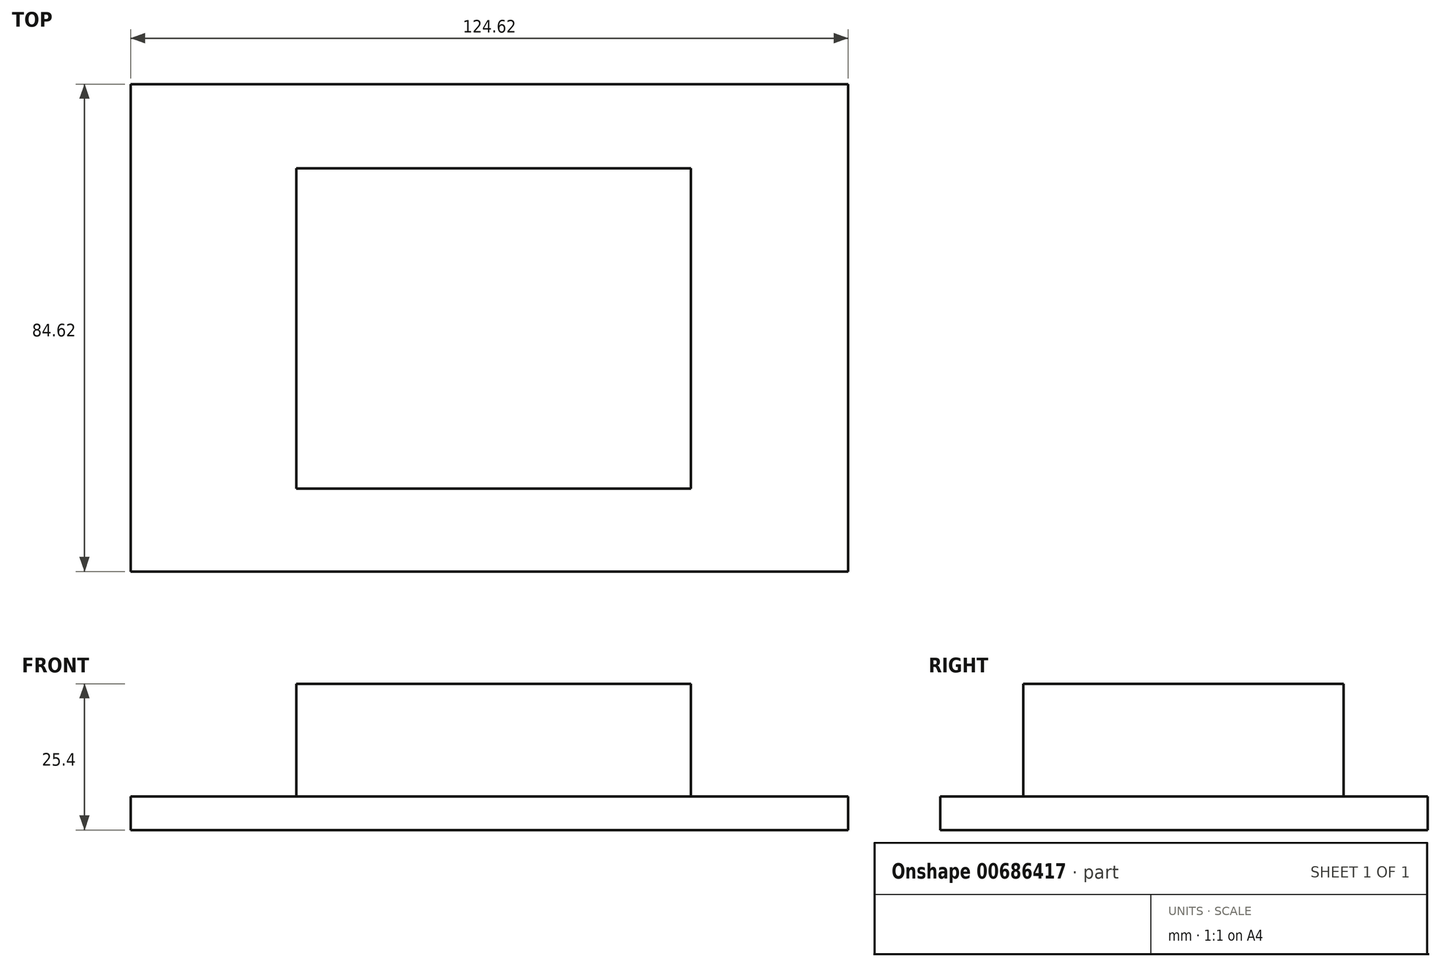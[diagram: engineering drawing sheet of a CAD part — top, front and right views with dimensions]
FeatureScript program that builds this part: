
annotation { "Feature Type Name" : "Feature", "Feature Type Description" : "" }
export const myFeature = defineFeature(function(context is Context, id is Id, definition is map)
    precondition{}
    {
        {
            var Q0;
            Q0=qCreatedBy(makeId("Top.planeOp"),FACE);
            var sketch = newSketch(context, id + "F0", { "sketchPlane" : qUnion([Q0])});
            skLineSegment(sketch, "E0", {"start": v(-37.41, 23.74) * mm, "end": v(-37.41, -32.38) * mm});
            skLineSegment(sketch, "E1", {"start": v(-37.41, -32.38) * mm, "end": v(31.08, -32.38) * mm});
            skLineSegment(sketch, "E2", {"start": v(31.08, -32.1) * mm, "end": v(31.08, 24.03) * mm});
            skLineSegment(sketch, "E3", {"start": v(-37.41, 23.74) * mm, "end": v(31.08, 24.03) * mm});
            skSolve(sketch);
        }
        {
            var Q0;
            Q0=sQuery(id+"F0.wireOp",EDGE,"E2");
            var Q1;
            Q1=sQuery(id+"F0.wireOp",EDGE,"E1");
            var Q2;
            Q2=sQuery(id+"F0.wireOp",EDGE,"E3");
            var Q3;
            Q3=sQuery(id+"F0.wireOp",EDGE,"E0");
            extrude(context, id + "F1", {"bodyType" : ToolBodyType.SURFACE, "surfaceEntities" : qUnion([Q0, Q1, Q2, Q3]), "depth" : 25.4 * mm, "offsetDistance" : 25.4 * mm});
        }
        {
            var Q0;
            Q0=qCreatedBy(makeId("Top.planeOp"),FACE);
            var sketch = newSketch(context, id + "F2", { "sketchPlane" : qUnion([Q0])});
            skLineSegment(sketch, "E4", {"start": v(-66.2, 32.95) * mm, "end": v(-66.2, -46.77) * mm});
            skLineSegment(sketch, "E5", {"start": v(-66.2, -46.77) * mm, "end": v(51.8, -46.77) * mm});
            skLineSegment(sketch, "E6", {"start": v(51.8, -46.77) * mm, "end": v(58.42, -46.77) * mm});
            skLineSegment(sketch, "E7", {"start": v(58.42, -46.77) * mm, "end": v(58.42, 37.85) * mm});
            skLineSegment(sketch, "E8", {"start": v(58.42, 37.85) * mm, "end": v(-66.2, 37.85) * mm});
            skLineSegment(sketch, "E9", {"start": v(-66.2, 32.95) * mm, "end": v(-66.2, 37.85) * mm});
            skSolve(sketch);
        }
        {
            var Q0;
            Q0=makeQuery(id+"F2.imprint","IMPRINT",FACE,{"disambiguationData":[TD([[makeQuery(id+"F2.imprint","IMPRINT",EDGE,{"derivedFrom":sQuery(id+"F2.wireOp",EDGE,"E4")}),1.0]])]});
            extrude(context, id + "F3", {"entities" : qUnion([Q0]), "depth" : 5.84 * mm, "offsetDistance" : 25.4 * mm});
        }
        {
            var Q0;
            Q0=makeQuery(id+"F1.opExtrude","SWEPT_FACE",FACE,{"disambiguationData":[OSD([sQuery(id+"F0.wireOp",EDGE,"E1")])]});
            extrude(context, id + "F4", {"entities" : qUnion([Q0]), "operationType" : NewBodyOperationType.ADD, "oppositeDirection" : true, "depth" : 55.63 * mm, "offsetDistance" : 25.4 * mm});
        }
    });
